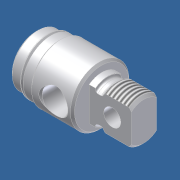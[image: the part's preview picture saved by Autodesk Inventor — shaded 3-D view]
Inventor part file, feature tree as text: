
AUTODESK INVENTOR PART (.ipt)
format: ipt  version: 2012 (Build 160160000, 160)  size: 266,240 bytes
history: native  units: in
note: dims shown in document units (in); Inventor stores cm internally (conversion verified against a paired STEP export)
features: other x155, sketch x7, revolve x5, extrude x2, thread x1
ambient origin geometry x8: Origin, YZ Plane, XZ Plane, XY Plane, X Axis, Y Axis, Z Axis, Center Point
bodies: Solid1 (feature_tree)
feature tree (170):
  other  "04P0010_rear_head"
  revolve  "Revolution1"  Angle=360.0deg
  revolve  "Revolution2"  [1 undecoded]
  thread  "Thread1"  [1 undecoded]
  extrude  "Extrusion1"  TaperAngle=360.0deg  [1 undecoded]
  revolve  "Revolution3"  [1 undecoded]
  revolve  "Revolution4"  [1 undecoded]
  revolve  "Revolution5"  [1 undecoded]
  extrude  "Extrusion2"  [1 undecoded]
  other  "c1_XY"
  other  "c1_YZ"
  other  "c1_ZX"
  other  "c1_X"
  other  "c1_Y"
  other  "c1_Z"
  other  "c1_Center"
  other  "cc1_XY"
  other  "cc1_YZ"
  other  "cc1_ZX"
  other  "cc1_X"
  other  "cc1_Y"
  other  "cc1_Z"
  other  "cc1_Center"
  other  "c2_XY"
  other  "c2_YZ"
  other  "c2_ZX"
  other  "c2_X"
  other  "c2_Y"
  other  "c2_Z"
  other  "c2_Center"
  other  "cc2_XY"
  other  "cc2_YZ"
  other  "cc2_ZX"
  other  "cc2_X"
  other  "cc2_Y"
  other  "cc2_Z"
  other  "cc2_Center"
  other  "to_tube_XY"
  other  "to_tube_YZ"
  other  "to_tube_ZX"
  other  "to_tube_X"
  other  "to_tube_Y"
  other  "to_tube_Z"
  other  "to_tube_Center"
  other  "to_nut_XY"
  other  "to_nut_YZ"
  other  "to_nut_ZX"
  other  "to_nut_X"
  other  "to_nut_Y"
  other  "to_nut_Z"
  other  "to_nut_Center"
  other  "lovra1_XY"
  other  "lovra1_YZ"
  other  "lovra1_ZX"
  other  "lovra1_X"
  other  "lovra1_Y"
  other  "lovra1_Z"
  other  "lovra1_Center"
  other  "lovra2_XY"
  other  "lovra2_YZ"
  other  "lovra2_ZX"
  other  "lovra2_X"
  other  "lovra2_Y"
  other  "lovra2_Z"
  other  "lovra2_Center"
  other  "lovra3_XY"
  other  "lovra3_YZ"
  other  "lovra3_ZX"
  other  "lovra3_X"
  other  "lovra3_Y"
  other  "lovra3_Z"
  other  "lovra3_Center"
  other  "to_pin_XY"
  other  "to_pin_YZ"
  other  "to_pin_ZX"
  other  "to_pin_X"
  other  "to_pin_Y"
  other  "to_pin_Z"
  other  "to_pin_Center"
  other  "olen_XY"
  other  "olen_YZ"
  other  "olen_ZX"
  other  "olen_X"
  other  "olen_Y"
  other  "olen_Z"
  other  "olen_Center"
  other  "thd1_XY"
  other  "thd1_YZ"
  other  "thd1_ZX"
  other  "thd1_X"
  other  "thd1_Y"
  other  "thd1_Z"
  other  "thd1_Center"
  other  "p1_XY"
  other  "p1_YZ"
  other  "p1_ZX"
  other  "p1_X"
  other  "p1_Y"
  other  "p1_Z"
  other  "p1_Center"
  other  "thd2_XY"
  other  "thd2_YZ"
  other  "thd2_ZX"
  other  "thd2_X"
  other  "thd2_Y"
  other  "thd2_Z"
  other  "thd2_Center"
  other  "p2_XY"
  other  "p2_YZ"
  other  "p2_ZX"
  other  "p2_X"
  other  "p2_Y"
  other  "p2_Z"
  other  "p2_Center"
  other  "port2_XY"
  other  "port2_YZ"
  other  "port2_ZX"
  other  "port2_X"
  other  "port2_Y"
  other  "port2_Z"
  other  "port2_Center"
  other  "port_XY"
  other  "port_YZ"
  other  "port_ZX"
  other  "port_X"
  other  "port_Y"
  other  "port_Z"
  other  "port_Center"
  other  "1_XY"
  other  "1_YZ"
  other  "1_ZX"
  other  "1_X"
  other  "1_Y"
  other  "1_Z"
  other  "1_Center"
  other  "lovra21_XY"
  other  "lovra21_YZ"
  other  "lovra21_ZX"
  other  "lovra21_X"
  other  "lovra21_Y"
  other  "lovra21_Z"
  other  "lovra21_Center"
  other  "lovra22_XY"
  other  "lovra22_YZ"
  other  "lovra22_ZX"
  other  "lovra22_X"
  other  "lovra22_Y"
  other  "lovra22_Z"
  other  "lovra22_Center"
  other  "to_screw_XY"
  other  "to_screw_YZ"
  other  "to_screw_ZX"
  other  "to_screw_X"
  other  "to_screw_Y"
  other  "to_screw_Z"
  other  "to_screw_Center"
  other  "to_mounting_bracket_XY"
  other  "to_mounting_bracket_YZ"
  other  "to_mounting_bracket_ZX"
  other  "to_mounting_bracket_X"
  other  "to_mounting_bracket_Y"
  other  "to_mounting_bracket_Z"
  other  "to_mounting_bracket_Center"
  sketch  "Sketch_8"  dims[d0=360.0deg d1=360.0deg]
  sketch  "Sketch_15"  dims[d9=0.5587in d10=0.0in]
  sketch  "Sketch_9"  dims[d2=0.4208in d3=0.0in d4=0.625in d5=0.0in d6=360.0deg]
  sketch  "Sketch_13"  dims[d7=360.0deg d8=360.0deg]
  sketch  "Sketch_19"
  sketch  "Sketch_24"
  sketch  "Sketch_43"
note: 7 required parameter values undecoded (feature->parameter linkage not recoverable at this tier; creation-order binding heuristic only, values carry confidence <= 0.55)